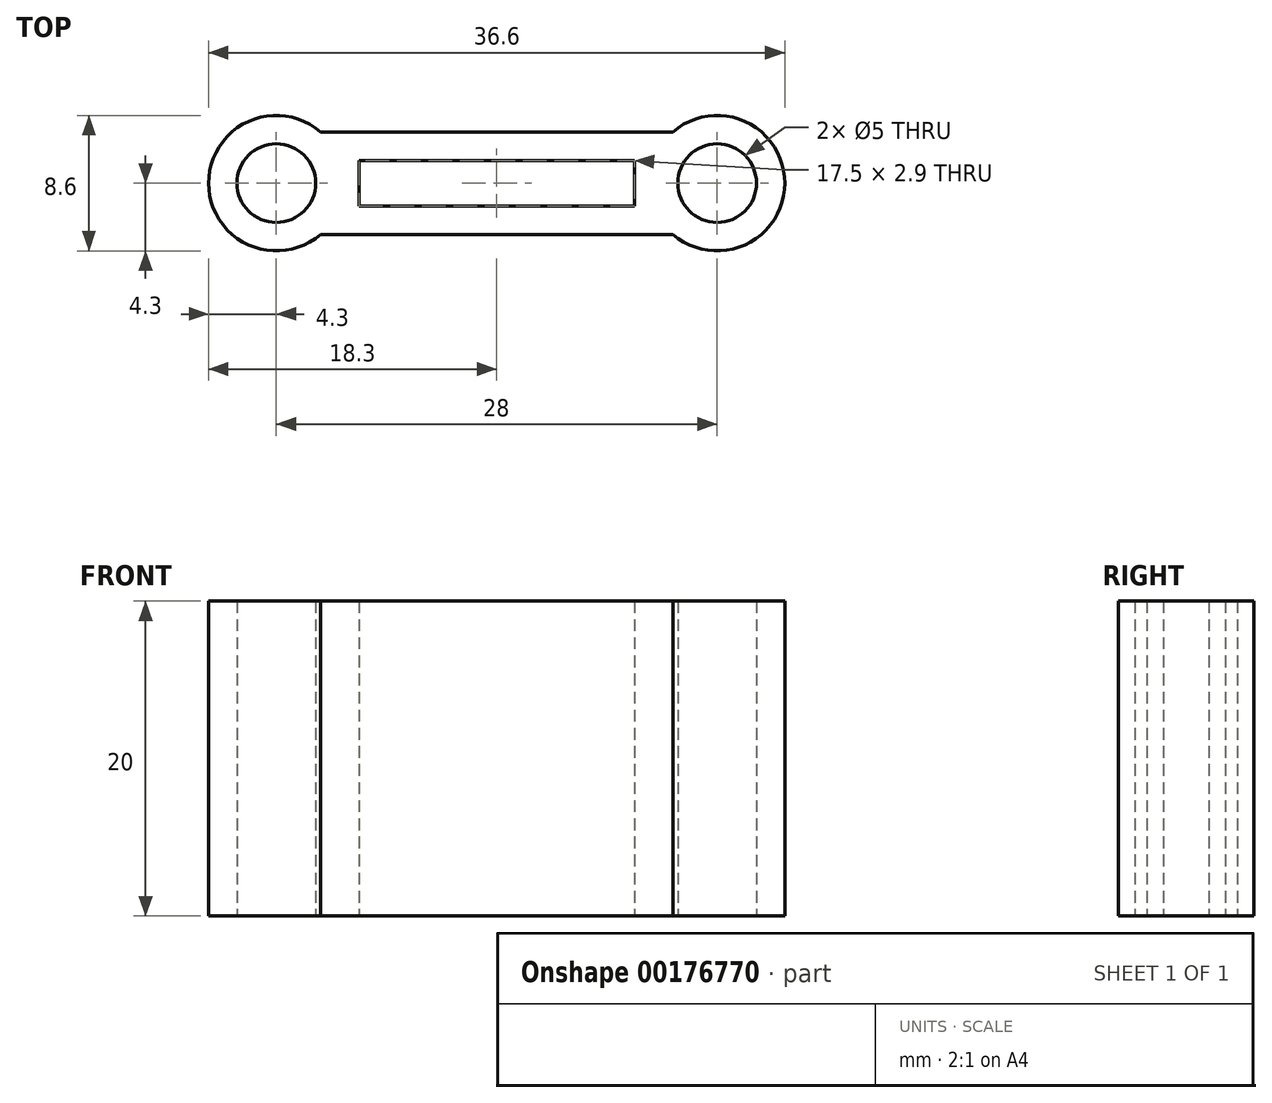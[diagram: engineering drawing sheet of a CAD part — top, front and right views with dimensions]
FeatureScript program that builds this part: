
annotation { "Feature Type Name" : "Feature", "Feature Type Description" : "" }
export const myFeature = defineFeature(function(context is Context, id is Id, definition is map)
    precondition{}
    {
        {
            assignVariable(context, id + "F0", {"name" : "pieceHeight", "anyValue" : 20});
        }
        {
            var Q0;
            Q0=qCreatedBy(makeId("Top.planeOp"),FACE);
            var sketch = newSketch(context, id + "F1", { "sketchPlane" : qUnion([Q0])});
            skCircle(sketch, "E0", {"center": v(-14, 0) * mm, "radius": 2.5 * mm});
            skCircle(sketch, "E1", {"center": v(14, 0) * mm, "radius": 2.5 * mm});
            skCircle(sketch, "E2.0", {"center": v(-14, 0) * mm, "radius": 4.3 * mm});
            skCircle(sketch, "E3.0", {"center": v(14, 0) * mm, "radius": 4.3 * mm});
            skLineSegment(sketch, "E4", {"start": v(-14, 0) * mm, "end": v(14, 0) * mm, "construction": true});
            skLineSegment(sketch, "E5.bottom", {"start": v(-8.75, 1.45) * mm, "end": v(8.75, 1.45) * mm});
            skLineSegment(sketch, "E5.top", {"start": v(-8.75, -1.45) * mm, "end": v(8.75, -1.45) * mm});
            skLineSegment(sketch, "E5.left", {"start": v(-8.75, 1.45) * mm, "end": v(-8.75, -1.45) * mm});
            skLineSegment(sketch, "E5.right", {"start": v(8.75, 1.45) * mm, "end": v(8.75, -1.45) * mm});
            skPoint(sketch, "E5.middle", {"position": v(0, 0) * mm});
            skLineSegment(sketch, "E6", {"start": v(-11.18, 3.25) * mm, "end": v(11.18, 3.25) * mm});
            skLineSegment(sketch, "E7", {"start": v(-11.18, -3.25) * mm, "end": v(11.18, -3.25) * mm});
            skSolve(sketch);
        }
        {
            var Q0;
            Q0=qSketchRegion(id+"F1",true);
            extrude(context, id + "F2", {"entities" : qUnion([Q0]), "depth" : (getVariable(context, 'pieceHeight')) * mm});
        }
    });
